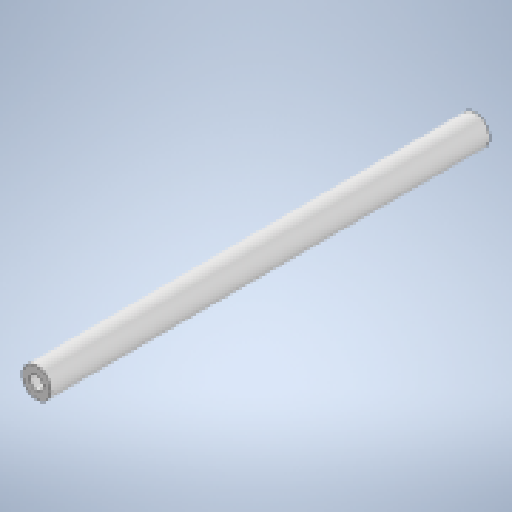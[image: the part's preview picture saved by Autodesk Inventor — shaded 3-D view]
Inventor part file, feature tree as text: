
AUTODESK INVENTOR PART (.ipt)
format: ipt  version: 2023 (Build 270158000, 158)  size: 256,000 bytes
history: native  units: mm
features: extrude x3, sketch x3
ambient origin geometry x8: Origin, YZ Plane, XZ Plane, XY Plane, X Axis, Y Axis, Z Axis, Center Point
bodies: Solid1 (feature_tree)
feature tree (6):
  extrude  "Extrusion1"  Depth=75.0mm TaperAngle=0.0deg
  extrude  "Extrusion2"  Depth=20.0mm TaperAngle=0.0deg
  extrude  "Extrusion3"  [1 undecoded]
  sketch  "Sketch1"  dims[d0=5.0mm d1=75.0mm d2=0.0mm]
  sketch  "Sketch2"  dims[d3=2.05mm d4=20.0mm d5=0.0mm]
  sketch  "Sketch3"  dims[d6=20.0mm d7=0.0mm]
note: 1 required parameter value undecoded (feature->parameter linkage not recoverable at this tier; creation-order binding heuristic only, values carry confidence <= 0.55)
